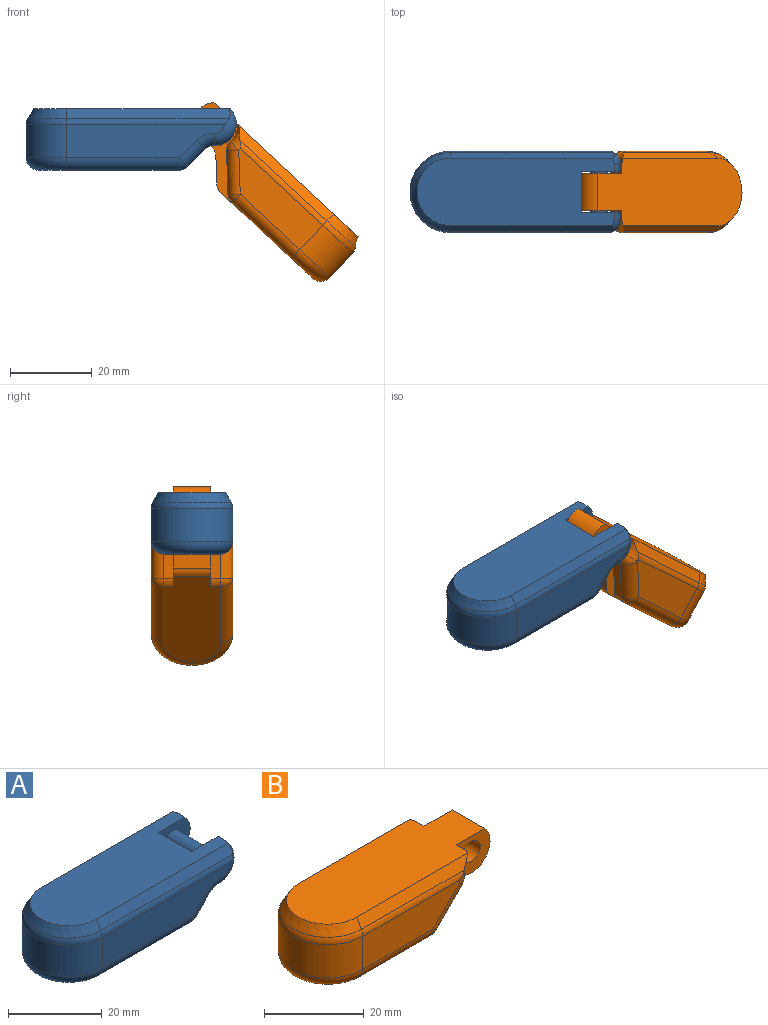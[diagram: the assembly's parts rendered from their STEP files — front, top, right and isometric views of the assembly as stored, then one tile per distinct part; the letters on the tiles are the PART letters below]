
ASSEMBLY  parts=2 mates=1
PART A: 37 faces, bbox 52.5x21.8x15.4 mm
  f0: plane 10x4.6mm, normal (0.71,0,-0.71), area 65mm2, adj f3,f7,f35,f36
  f1: plane 4.2x4.2mm, normal (0.71,0,-0.71), area 11.9mm2, adj f7,f28,f31,f34
  f2: plane 4.2x4.2mm, normal (0.71,0,-0.71), area 11.9mm2, adj f3,f17,f19,f20
  f3: plane 17.8x15mm, normal (0,-1,0), area 96.4mm2, adj f0,f2,f8,f9,f10,f11,f13,f17
  f4: plane 38.55x8.2mm, normal (0,1,0), area 267.6mm2, adj f5,f18,f20,f21,f23,f24
  f5: cylinder r=10mm len=20mm, axis (0,0,-1), area 257.5mm2, adj f4,f6,f25,f26
  f6: plane 38.55x8.2mm, normal (0,-1,0), area 267.6mm2, adj f5,f27,f29,f30,f33,f34
  f7: plane 17.8x15mm, normal (0,1,0), area 96.4mm2, adj f0,f1,f8,f9,f10,f12,f13,f28
  f8: plane 48.42x16.69mm, normal (0,0,1), area 688.1mm2, adj f3,f7,f11,f12,f13,f14,f15,f16
  f9: plane 34.51x14mm, normal (0,0,-1), area 424.6mm2, adj f3,f7,f19,f24,f26,f28,f29,f35
  f10: cylinder r=2.1mm len=10mm, axis (0,1,0), area 131.9mm2, adj f3,f7
  f11: cylinder r=5.3mm len=9.05mm, axis (0,-1,0), area 25.4mm2, adj f3,f8,f17,f21
  f12: cylinder r=5.3mm len=9.05mm, axis (0,1,0), area 25.4mm2, adj f7,f8,f30,f31
  f13: cylinder r=5.7mm len=10mm, axis (0,1,0), area 65.6mm2, adj f3,f7,f8,f36
  f14: plane 40.05x2.3mm, normal (0,-0.87,0.5), area 106.2mm2, adj f8,f15,f27,f30
  f15: cone r=8.27mm half-angle=30deg, axis (0,0,-1), area 74.7mm2, adj f8,f14,f16,f25
  f16: plane 40.05x2.3mm, normal (0,0.87,0.5), area 106.2mm2, adj f8,f15,f21,f23
  f17: cylinder r=3mm len=2.23mm, axis (0,-1,0), area 4.9mm2, adj f2,f3,f11,f18
  f18: torus R=6mm, axis (0,-1,0), area 15.8mm2, adj f4,f17,f20,f21
  f19: cylinder r=3mm len=2.12mm, axis (0,1,0), area 4.7mm2, adj f2,f3,f9,f22
  f20: cylinder r=3mm len=6.32mm, axis (0.71,0,0.71), area 28mm2, adj f2,f4,f18,f22
  f21: torus R=2.3mm, axis (0,-1,0), area 43.5mm2, adj f4,f8,f11,f16,f18,f23
  f22: sphere r=3mm, area 7.1mm2, adj f19,f20,f24
  f23: cylinder r=3mm len=39.77mm, axis (-1,0,0), area 61.5mm2, adj f4,f16,f21,f25
  f24: cylinder r=3mm len=27.51mm, axis (-1,0,0), area 129.6mm2, adj f4,f9,f22,f26
  f25: torus R=7mm, axis (0,0,1), area 48.7mm2, adj f5,f15,f23,f27
  f26: torus R=7mm, axis (0,0,1), area 131.9mm2, adj f5,f9,f24,f29
  f27: cylinder r=3mm len=39.77mm, axis (1,0,0), area 61.5mm2, adj f6,f14,f25,f30
  f28: cylinder r=3mm len=2.12mm, axis (0,1,0), area 4.7mm2, adj f1,f7,f9,f32
  f29: cylinder r=3mm len=27.51mm, axis (1,0,0), area 129.6mm2, adj f6,f9,f26,f32
  f30: torus R=2.3mm, axis (0,1,0), area 43.5mm2, adj f6,f8,f12,f14,f27,f33
  f31: cylinder r=3mm len=2.23mm, axis (0,1,0), area 4.9mm2, adj f1,f7,f12,f33
  f32: sphere r=3mm, area 7.1mm2, adj f28,f29,f34
  f33: torus R=6mm, axis (0,1,0), area 15.8mm2, adj f6,f30,f31,f34
  f34: cylinder r=3mm len=6.32mm, axis (0.71,0,0.71), area 28mm2, adj f1,f6,f32,f33
  f35: cylinder r=3mm len=10mm, axis (0,-1,0), area 23.6mm2, adj f0,f3,f7,f9
  f36: cylinder r=3mm len=10mm, axis (0,1,0), area 36.6mm2, adj f0,f3,f7,f13
PART B: 37 faces, bbox 52.5x21.8x19.1 mm
  f0: plane 9.2x4.9mm, normal (0.71,0,-0.71), area 63.7mm2, adj f3,f4,f35,f36
  f1: cylinder r=5.3mm len=9.2mm, axis (0,1,0), area 135.2mm2, adj f4,f5,f35,f36
  f2: cylinder r=2.5mm len=9.2mm, axis (0,1,0), area 144.5mm2, adj f35,f36
  f3: cylinder r=3mm len=9.2mm, axis (0,1,0), area 21.7mm2, adj f0,f6,f35,f36
  f4: cylinder r=3mm len=9.2mm, axis (0,1,0), area 33.2mm2, adj f0,f1,f35,f36
  f5: plane 48.38x16.65mm, normal (0,0,1), area 709.5mm2, adj f1,f12,f13,f14,f15,f16,f31,f33
  f6: plane 30.76x14mm, normal (0,0,-1), area 391.6mm2, adj f3,f19,f25,f27,f28,f30,f35,f36
  f7: plane 7.57x7.57mm, normal (0.71,0,-0.71), area 25.7mm2, adj f17,f19,f20,f35
  f8: plane 27.58x8.2mm, normal (0,1,0), area 197.4mm2, adj f9,f18,f20,f25,f33
  f9: cylinder r=10mm len=20mm, axis (0,0,-1), area 257.5mm2, adj f8,f10,f21,f28
  f10: plane 27.58x8.2mm, normal (0,-1,0), area 197.4mm2, adj f9,f23,f26,f30,f31
  f11: plane 7.57x7.57mm, normal (0.71,0,-0.71), area 25.7mm2, adj f24,f26,f27,f36
  f12: cylinder r=5.7mm len=4.2mm, axis (0,-1,0), area 10.9mm2, adj f5,f17,f33,f35
  f13: cylinder r=5.7mm len=4.2mm, axis (0,1,0), area 10.9mm2, adj f5,f24,f31,f36
  f14: plane 31.59x2.3mm, normal (0,0.87,0.5), area 80.9mm2, adj f5,f15,f18,f33
  f15: cone r=8.27mm half-angle=30deg, axis (0,0,-1), area 74.7mm2, adj f5,f14,f16,f21
  f16: plane 31.59x2.31mm, normal (0,-0.87,0.5), area 80.9mm2, adj f5,f15,f23,f31
  f17: cylinder r=3mm len=2.4mm, axis (0,-1,0), area 6.2mm2, adj f7,f12,f34,f35
  f18: cylinder r=3mm len=29.2mm, axis (-1,0,0), area 44.6mm2, adj f8,f14,f21,f33
  f19: cylinder r=3mm len=2.4mm, axis (0,1,0), area 5.7mm2, adj f6,f7,f22,f35
  f20: cylinder r=3mm len=9.69mm, axis (-0.71,0,-0.71), area 50.4mm2, adj f7,f8,f22,f34
  f21: torus R=7mm, axis (0,0,1), area 48.7mm2, adj f9,f15,f18,f23
  f22: sphere r=3mm, area 7.1mm2, adj f19,f20,f25
  f23: cylinder r=3mm len=29.2mm, axis (1,0,0), area 44.6mm2, adj f10,f16,f21,f31
  f24: cylinder r=3mm len=2.4mm, axis (0,1,0), area 6.2mm2, adj f11,f13,f32,f36
  f25: cylinder r=3mm len=20.01mm, axis (-1,0,0), area 94.3mm2, adj f6,f8,f22,f28
  f26: cylinder r=3mm len=9.69mm, axis (0.71,0,0.71), area 50.4mm2, adj f10,f11,f29,f32
  f27: cylinder r=3mm len=2.4mm, axis (0,1,0), area 5.7mm2, adj f6,f11,f29,f36
  f28: torus R=7mm, axis (0,0,1), area 131.9mm2, adj f6,f9,f25,f30
  f29: sphere r=3mm, area 7.1mm2, adj f26,f27,f30
  f30: cylinder r=3mm len=20.01mm, axis (1,0,0), area 94.3mm2, adj f6,f10,f28,f29
  f31: torus R=8.7mm, axis (0,1,0), area 13.7mm2, adj f5,f10,f13,f16,f23,f32
  f32: sphere r=3mm, area 7.8mm2, adj f24,f26,f31
  f33: torus R=8.7mm, axis (0,-1,0), area 13.7mm2, adj f5,f8,f12,f14,f18,f34
  f34: sphere r=3mm, area 7.5mm2, adj f17,f20,f33
  f35: plane 21.55x15mm, normal (0,1,0), area 96.5mm2, adj f0,f1,f2,f3,f4,f5,f6,f7
  f36: plane 21.55x15mm, normal (0,-1,0), area 96.5mm2, adj f0,f1,f2,f3,f4,f5,f6,f11
PLACE A t=(10.51,2.19,13.15)mm fixed
PLACE B rot(axis=(0.37,0,0.93),180deg) t=(39.62,2.19,1.68)mm
MATE revolute A.f10 <-> B.f1  axis (0,1,0) through (31.76,2.19,24.4)mm
